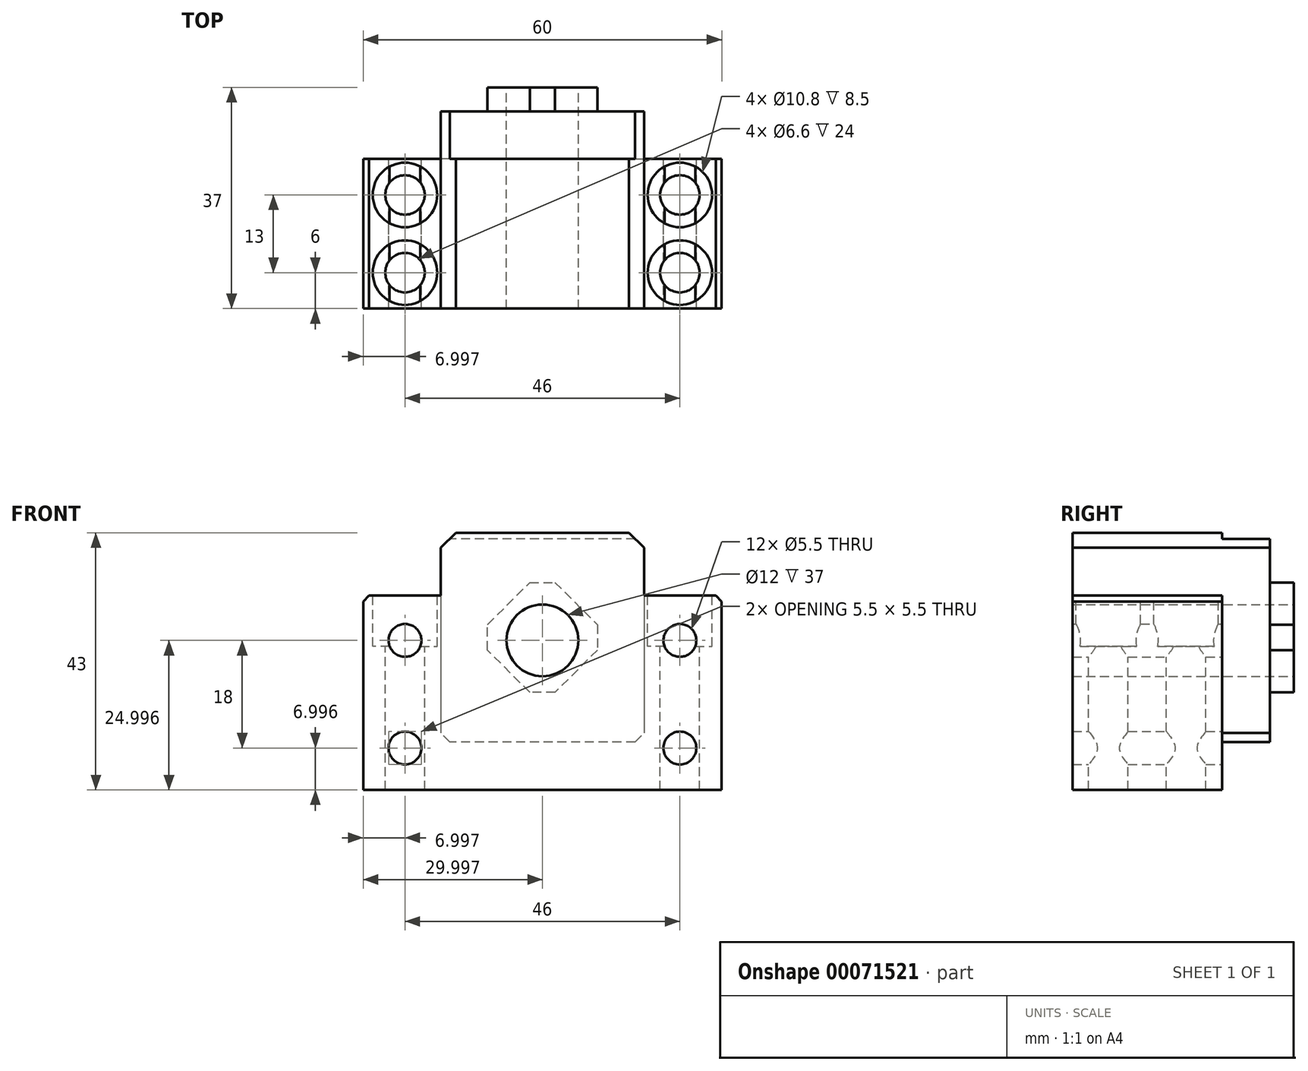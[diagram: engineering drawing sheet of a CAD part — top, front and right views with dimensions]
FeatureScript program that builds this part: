
annotation { "Feature Type Name" : "Feature", "Feature Type Description" : "" }
export const myFeature = defineFeature(function(context is Context, id is Id, definition is map)
    precondition{}
    {
        {
            var Q0;
            Q0=qCreatedBy(makeId("Front.planeOp"),FACE);
            var sketch = newSketch(context, id + "F0", { "sketchPlane" : qUnion([Q0])});
            skLineSegment(sketch, "E0.bottom", {"start": v(-37.23, 0.43) * mm, "end": v(-26.73, 0.43) * mm});
            skLineSegment(sketch, "E0.top", {"start": v(-39.73, -32.07) * mm, "end": v(20.27, -32.07) * mm});
            skLineSegment(sketch, "E0.left", {"start": v(-39.73, 15.43) * mm, "end": v(-39.73, -32.07) * mm});
            skLineSegment(sketch, "E0.right", {"start": v(20.27, 15.43) * mm, "end": v(20.27, -32.07) * mm});
            skCircle(sketch, "E1", {"center": v(-9.73, -7.07) * mm, "radius": 6 * mm});
            skLineSegment(sketch, "E2.bottom", {"start": v(-26.73, 10.93) * mm, "end": v(7.27, 10.93) * mm});
            skLineSegment(sketch, "E2.left", {"start": v(-26.73, 10.93) * mm, "end": v(-26.73, 0.43) * mm});
            skLineSegment(sketch, "E2.right", {"start": v(7.27, 10.93) * mm, "end": v(7.27, 0.43) * mm});
            skLineSegment(sketch, "E3.trimOffspring", {"start": v(7.27, 0.43) * mm, "end": v(45.77, 0.43) * mm});
            skCircle(sketch, "E4", {"center": v(-32.73, -7.07) * mm, "radius": 2.75 * mm});
            skCircle(sketch, "E5", {"center": v(-32.73, -25.07) * mm, "radius": 2.75 * mm});
            skCircle(sketch, "E6", {"center": v(13.27, -25.07) * mm, "radius": 2.75 * mm});
            skCircle(sketch, "E7", {"center": v(13.27, -7.07) * mm, "radius": 2.75 * mm});
            skLineSegment(sketch, "E8.top", {"start": v(-39.73, 0.43) * mm, "end": v(-33.45, 0.43) * mm});
            skLineSegment(sketch, "E8.left", {"start": v(-39.73, 0.43) * mm, "end": v(-39.73, 9.55) * mm});
            skLineSegment(sketch, "E9.bottom", {"start": v(20.27, 0.43) * mm, "end": v(42.4, 0.43) * mm});
            skLineSegment(sketch, "E9.right", {"start": v(20.27, 11.22) * mm, "end": v(20.27, 0.43) * mm});
            skSolve(sketch);
        }
        {
            var Q0;
            {var subQ0=sQuery(id+"F0.wireOp",EDGE,"E0.bottom");Q0=makeQuery(id+"F0.imprint","IMPRINT",FACE,{"disambiguationData":[TD([[makeQuery(id+"F0.imprint","IMPRINT",EDGE,{"derivedFrom":subQ0}),-1.0]])]});}
            extrude(context, id + "F1", {"entities" : qUnion([Q0]), "depth" : 25 * mm});
        }
        {
            var Q0;
            Q0=makeQuery(id+"F1.opExtrude","SWEPT_EDGE",EDGE,{"disambiguationData":[OSD([sQuery(id+"F0.wireOp",EDGE,"E2.bottom"),sQuery(id+"F0.wireOp",EDGE,"E2.left")])]});
            var Q1;
            Q1=makeQuery(id+"F1.opExtrude","SWEPT_EDGE",EDGE,{"disambiguationData":[OSD([sQuery(id+"F0.wireOp",EDGE,"E2.bottom"),sQuery(id+"F0.wireOp",EDGE,"E2.right")])]});
            chamfer(context, id + "F2", {"entities" : qUnion([Q0, Q1]), "width" : 2.5 * mm, "tangentPropagation" : true});
        }
        {
            var Q0;
            Q0=makeQuery(id+"F1.opExtrude","SWEPT_FACE",FACE,{"disambiguationData":[OSD([sQuery(id+"F0.wireOp",EDGE,"E0.bottom")])]});
            var sketch = newSketch(context, id + "F3", { "sketchPlane" : qUnion([Q0])});
            skCircle(sketch, "E10", {"center": v(13.27, -19) * mm, "radius": 5.4 * mm});
            skCircle(sketch, "E11", {"center": v(-32.73, -6) * mm, "radius": 3.3 * mm});
            skCircle(sketch, "E12", {"center": v(13.27, -6) * mm, "radius": 5.4 * mm});
            skCircle(sketch, "E13", {"center": v(13.27, -19) * mm, "radius": 3.3 * mm});
            skCircle(sketch, "E14", {"center": v(-32.73, -19) * mm, "radius": 3.3 * mm});
            skCircle(sketch, "E15", {"center": v(13.27, -6) * mm, "radius": 3.3 * mm});
            skCircle(sketch, "E16", {"center": v(-32.73, -6) * mm, "radius": 5.4 * mm});
            skCircle(sketch, "E17", {"center": v(-32.73, -19) * mm, "radius": 5.4 * mm});
            skSolve(sketch);
        }
        {
            var Q0;
            Q0=makeQuery(id+"F3.imprint","IMPRINT",FACE,{"disambiguationData":[TD([[makeQuery(id+"F3.imprint","IMPRINT",EDGE,{"derivedFrom":sQuery(id+"F3.wireOp",EDGE,"E10")}),1.0]])]});
            var Q1;
            Q1=makeQuery(id+"F3.imprint","IMPRINT",FACE,{"disambiguationData":[TD([[makeQuery(id+"F3.imprint","IMPRINT",EDGE,{"derivedFrom":sQuery(id+"F3.wireOp",EDGE,"E12")}),1.0]])]});
            var Q2;
            Q2=makeQuery(id+"F3.imprint","IMPRINT",FACE,{"disambiguationData":[TD([[makeQuery(id+"F3.imprint","IMPRINT",EDGE,{"derivedFrom":sQuery(id+"F3.wireOp",EDGE,"E11")}),-1.0]])]});
            var Q3;
            Q3=makeQuery(id+"F3.imprint","IMPRINT",FACE,{"disambiguationData":[TD([[makeQuery(id+"F3.imprint","IMPRINT",EDGE,{"derivedFrom":sQuery(id+"F3.wireOp",EDGE,"E14")}),-1.0]])]});
            extrude(context, id + "F4", {"entities" : qUnion([Q0, Q1, Q2, Q3]), "operationType" : NewBodyOperationType.REMOVE, "oppositeDirection" : true, "depth" : 8.5 * mm});
        }
        {
            var Q0;
            Q0=makeQuery(id+"F4.boolean.opBoolean","SPLIT",FACE,{"disambiguationData":[TD([makeQuery(id+"F4.opExtrude","SWEPT_FACE",FACE,{"disambiguationData":[OSD([sQuery(id+"F3.wireOp",EDGE,"E13")])]})])],"derivedFrom":makeQuery(id+"F1.opExtrude","SWEPT_FACE",FACE,{"disambiguationData":[OSD([sQuery(id+"F0.wireOp",EDGE,"E3.trimOffspring"),sQuery(id+"F0.wireOp",EDGE,"E9.bottom")])]})});
            var Q1;
            Q1=makeQuery(id+"F4.boolean.opBoolean","SPLIT",FACE,{"disambiguationData":[TD([makeQuery(id+"F4.opExtrude","SWEPT_FACE",FACE,{"disambiguationData":[OSD([sQuery(id+"F3.wireOp",EDGE,"E15")])]})])],"derivedFrom":makeQuery(id+"F1.opExtrude","SWEPT_FACE",FACE,{"disambiguationData":[OSD([sQuery(id+"F0.wireOp",EDGE,"E3.trimOffspring"),sQuery(id+"F0.wireOp",EDGE,"E9.bottom")])]})});
            var Q2;
            Q2=makeQuery(id+"F4.boolean.opBoolean","SPLIT",FACE,{"disambiguationData":[TD([makeQuery(id+"F4.opExtrude","SWEPT_FACE",FACE,{"disambiguationData":[OSD([sQuery(id+"F3.wireOp",EDGE,"E11")])]})])],"derivedFrom":makeQuery(id+"F1.opExtrude","SWEPT_FACE",FACE,{"disambiguationData":[OSD([sQuery(id+"F0.wireOp",EDGE,"E0.bottom"),sQuery(id+"F0.wireOp",EDGE,"E8.top")])]})});
            var Q3;
            Q3=makeQuery(id+"F4.boolean.opBoolean","SPLIT",FACE,{"disambiguationData":[TD([makeQuery(id+"F4.opExtrude","SWEPT_FACE",FACE,{"disambiguationData":[OSD([sQuery(id+"F3.wireOp",EDGE,"E14")])]})])],"derivedFrom":makeQuery(id+"F1.opExtrude","SWEPT_FACE",FACE,{"disambiguationData":[OSD([sQuery(id+"F0.wireOp",EDGE,"E0.bottom"),sQuery(id+"F0.wireOp",EDGE,"E8.top")])]})});
            extrude(context, id + "F5", {"entities" : qUnion([Q0, Q1, Q2, Q3]), "operationType" : NewBodyOperationType.REMOVE, "endBound" : BoundingType.THROUGH_ALL, "oppositeDirection" : true, "depth" : 25 * mm});
        }
        {
            var Q0;
            Q0=makeQuery(id+"F1.opExtrude","SWEPT_EDGE",EDGE,{"disambiguationData":[OSD([sQuery(id+"F0.wireOp",EDGE,"E9.bottom"),sQuery(id+"F0.wireOp",EDGE,"E9.right")])]});
            var Q1;
            Q1=makeQuery(id+"F1.opExtrude","SWEPT_EDGE",EDGE,{"disambiguationData":[OSD([sQuery(id+"F0.wireOp",EDGE,"E8.top"),sQuery(id+"F0.wireOp",EDGE,"E8.left")])]});
            var Q2;
            Q2=makeQuery(id+"F1.opExtrude","SWEPT_EDGE",EDGE,{"disambiguationData":[OSD([sQuery(id+"F0.wireOp",EDGE,"E0.right"),sQuery(id+"F0.wireOp",EDGE,"E3.trimOffspring")])]});
            chamfer(context, id + "F6", {"entities" : qUnion([Q0, Q1, Q2]), "width" : 1 * mm, "tangentPropagation" : true});
        }
        {
            var Q0;
            Q0=makeQuery(id+"F1.opExtrude","CAP_FACE",FACE,{"disambiguationData":[OSD([sQuery(id+"F0.wireOp",EDGE,"E0.bottom"),sQuery(id+"F0.wireOp",EDGE,"E0.top"),sQuery(id+"F0.wireOp",EDGE,"E0.left"),sQuery(id+"F0.wireOp",EDGE,"E0.right"),sQuery(id+"F0.wireOp",EDGE,"E1"),sQuery(id+"F0.wireOp",EDGE,"E2.bottom"),sQuery(id+"F0.wireOp",EDGE,"E2.left"),sQuery(id+"F0.wireOp",EDGE,"E2.right"),sQuery(id+"F0.wireOp",EDGE,"E3.trimOffspring"),sQuery(id+"F0.wireOp",EDGE,"E4"),sQuery(id+"F0.wireOp",EDGE,"E5"),sQuery(id+"F0.wireOp",EDGE,"E6"),sQuery(id+"F0.wireOp",EDGE,"E7"),sQuery(id+"F0.wireOp",EDGE,"E8.top"),sQuery(id+"F0.wireOp",EDGE,"E8.left"),sQuery(id+"F0.wireOp",EDGE,"E9.bottom"),sQuery(id+"F0.wireOp",EDGE,"E9.right")])],"isStart":true});
            var sketch = newSketch(context, id + "F7", { "sketchPlane" : qUnion([Q0])});
            skLineSegment(sketch, "E18.bottom", {"start": v(-7.27, 9.93) * mm, "end": v(26.73, 9.93) * mm});
            skLineSegment(sketch, "E18.top", {"start": v(-7.27, -24.07) * mm, "end": v(26.73, -24.07) * mm});
            skLineSegment(sketch, "E18.left", {"start": v(-7.27, 9.93) * mm, "end": v(-7.27, -24.07) * mm});
            skLineSegment(sketch, "E18.right", {"start": v(26.73, 9.93) * mm, "end": v(26.73, -24.07) * mm});
            skCircle(sketch, "E19", {"center": v(9.73, -7.07) * mm, "radius": 6 * mm});
            skSolve(sketch);
        }
        {
            var Q0;
            Q0=qSketchRegion(id+"F7",true);
            extrude(context, id + "F8", {"entities" : qUnion([Q0]), "operationType" : NewBodyOperationType.ADD, "depth" : 8 * mm});
        }
        {
            var Q0;
            Q0=makeQuery(id+"F8.opExtrude","SWEPT_EDGE",EDGE,{"disambiguationData":[OSD([sQuery(id+"F7.wireOp",EDGE,"E18.bottom"),sQuery(id+"F7.wireOp",EDGE,"E18.left")])]});
            chamfer(context, id + "F9", {"entities" : qUnion([Q0]), "width" : 1.5 * mm, "tangentPropagation" : true});
        }
        {
            var Q0;
            Q0=makeQuery(id+"F8.opExtrude","SWEPT_EDGE",EDGE,{"disambiguationData":[OSD([sQuery(id+"F7.wireOp",EDGE,"E18.bottom"),sQuery(id+"F7.wireOp",EDGE,"E18.right")])]});
            var Q1;
            Q1=makeQuery(id+"F8.opExtrude","SWEPT_EDGE",EDGE,{"disambiguationData":[OSD([sQuery(id+"F7.wireOp",EDGE,"E18.top"),sQuery(id+"F7.wireOp",EDGE,"E18.left")])]});
            var Q2;
            Q2=makeQuery(id+"F8.opExtrude","SWEPT_EDGE",EDGE,{"disambiguationData":[OSD([sQuery(id+"F7.wireOp",EDGE,"E18.top"),sQuery(id+"F7.wireOp",EDGE,"E18.right")])]});
            chamfer(context, id + "F10", {"entities" : qUnion([Q0, Q1, Q2]), "width" : 1.5 * mm, "tangentPropagation" : true});
        }
        {
            var Q0;
            Q0=makeQuery(id+"F8.opExtrude","CAP_FACE",FACE,{"disambiguationData":[OSD([sQuery(id+"F7.wireOp",EDGE,"E18.bottom"),sQuery(id+"F7.wireOp",EDGE,"E18.top"),sQuery(id+"F7.wireOp",EDGE,"E18.left"),sQuery(id+"F7.wireOp",EDGE,"E18.right"),sQuery(id+"F7.wireOp",EDGE,"E19")])],"isStart":false});
            var sketch = newSketch(context, id + "F11", { "sketchPlane" : qUnion([Q0])});
            skLineSegment(sketch, "E20", {"start": v(-1.58, -6.57) * mm, "end": v(9.73, -17.89) * mm});
            skLineSegment(sketch, "E21", {"start": v(9.73, -17.89) * mm, "end": v(21.05, -6.57) * mm});
            skLineSegment(sketch, "E22", {"start": v(21.05, -6.57) * mm, "end": v(9.73, 4.74) * mm});
            skLineSegment(sketch, "E23", {"start": v(9.73, 4.74) * mm, "end": v(-1.58, -6.57) * mm});
            skSolve(sketch);
        }
        {
            var Q0;
            Q0=makeQuery(id+"F11.imprint","IMPRINT",FACE,{"disambiguationData":[TD([[makeQuery(id+"F11.imprint","IMPRINT",EDGE,{"derivedFrom":sQuery(id+"F11.wireOp",EDGE,"E20")}),1.0]])]});
            extrude(context, id + "F12", {"entities" : qUnion([Q0]), "operationType" : NewBodyOperationType.ADD, "depth" : 4 * mm});
        }
        {
            var Q0;
            Q0=makeQuery(id+"F12.opExtrude","SWEPT_EDGE",EDGE,{"disambiguationData":[OSD([sQuery(id+"F11.wireOp",EDGE,"E22"),sQuery(id+"F11.wireOp",EDGE,"E23")])]});
            var Q1;
            Q1=makeQuery(id+"F12.opExtrude","SWEPT_EDGE",EDGE,{"disambiguationData":[OSD([sQuery(id+"F11.wireOp",EDGE,"E20"),sQuery(id+"F11.wireOp",EDGE,"E23")])]});
            var Q2;
            Q2=makeQuery(id+"F12.opExtrude","SWEPT_EDGE",EDGE,{"disambiguationData":[OSD([sQuery(id+"F11.wireOp",EDGE,"E20"),sQuery(id+"F11.wireOp",EDGE,"E21")])]});
            var Q3;
            Q3=makeQuery(id+"F12.opExtrude","SWEPT_EDGE",EDGE,{"disambiguationData":[OSD([sQuery(id+"F11.wireOp",EDGE,"E21"),sQuery(id+"F11.wireOp",EDGE,"E22")])]});
            chamfer(context, id + "F13", {"entities" : qUnion([Q0, Q1, Q2, Q3]), "width" : 3 * mm, "tangentPropagation" : true});
        }
    });
